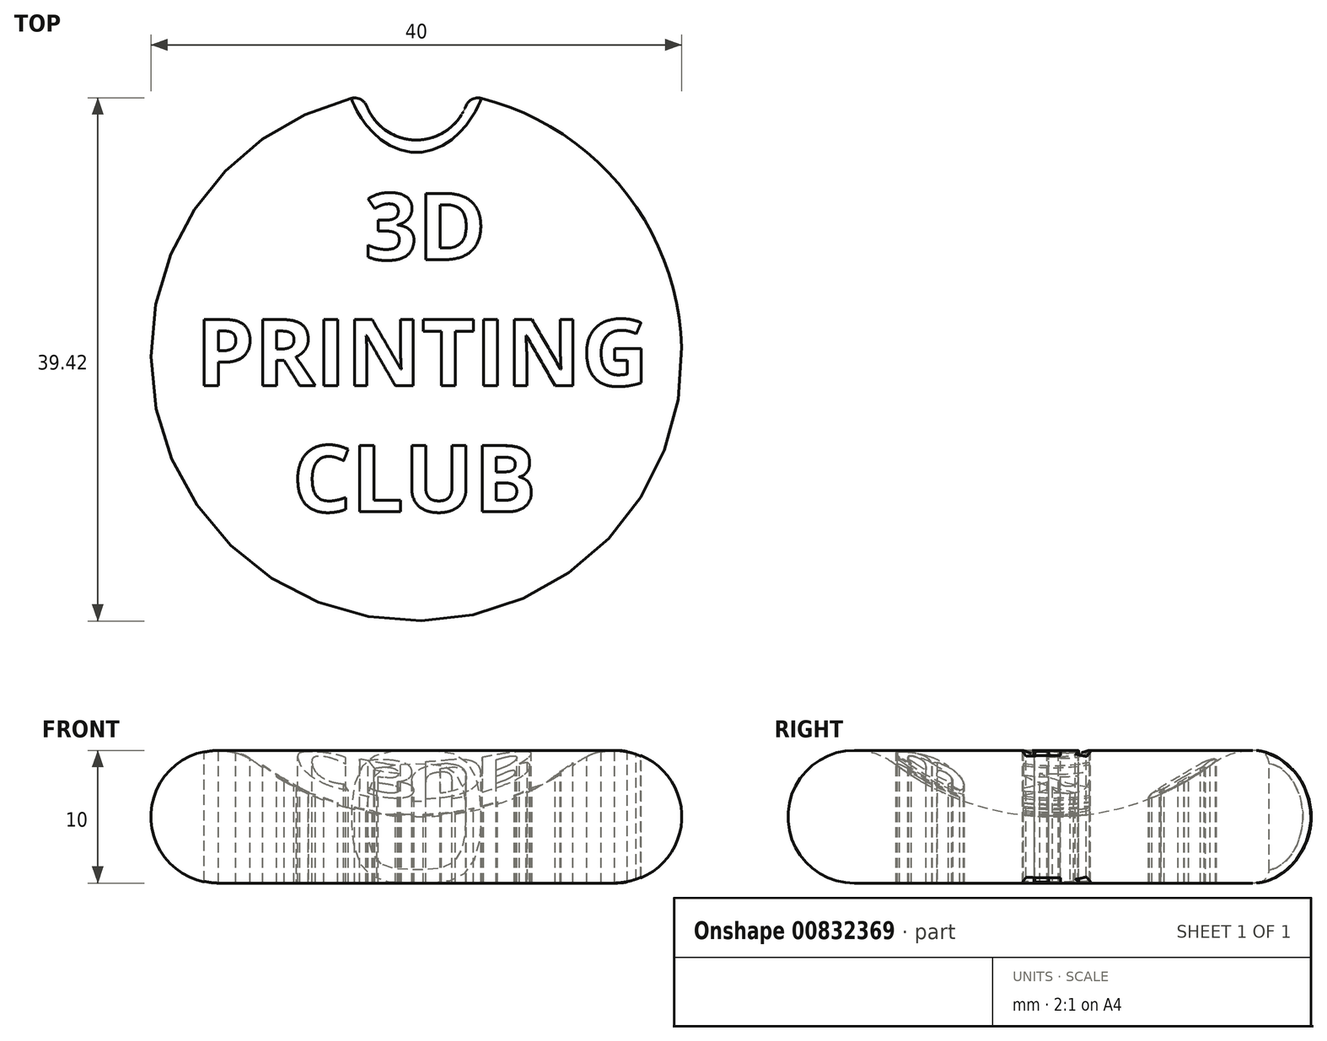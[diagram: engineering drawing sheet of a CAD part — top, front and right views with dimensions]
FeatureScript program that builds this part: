
annotation { "Feature Type Name" : "Feature", "Feature Type Description" : "" }
export const myFeature = defineFeature(function(context is Context, id is Id, definition is map)
    precondition{}
    {
        {
            var Q0;
            Q0=qCreatedBy(makeId("Front.planeOp"),FACE);
            var sketch = newSketch(context, id + "F0", { "sketchPlane" : qUnion([Q0])});
            skArc(sketch, "E0", {"start": v(-12, 9) * mm, "mid": v(-6.32, 6.03) * mm, "end": v(0, 5) * mm});
            skArc(sketch, "E1", {"start": v(-12, 9) * mm, "mid": v(-19.74, 6.58) * mm, "end": v(-15, 0) * mm});
            skLineSegment(sketch, "E2", {"start": v(0, 5) * mm, "end": v(0, 0) * mm});
            skLineSegment(sketch, "E3", {"start": v(0, 0) * mm, "end": v(-15, 0) * mm});
            skSolve(sketch);
        }
        {
            var Q0;
            Q0=makeQuery(id+"F0.imprint","IMPRINT",FACE,{"disambiguationData":[TD([[makeQuery(id+"F0.imprint","IMPRINT",EDGE,{"derivedFrom":sQuery(id+"F0.wireOp",EDGE,"E0")}),-1.0]])]});
            var Q1;
            Q1=sQuery(id+"F0.wireOp",EDGE,"E2");
            revolve(context, id + "F1", {"surfaceOperationType" : NewSurfaceOperationType.NEW, "entities" : qUnion([Q0]), "axis" : qUnion([Q1]), "revolveType" : RevolveType.FULL});
        }
        {
            var Q0;
            Q0=qCreatedBy(makeId("Top.planeOp"),FACE);
            cPlane(context, id + "F2", {"entities" : qUnion([Q0]), "cplaneType" : CPlaneType.OFFSET, "offset" : 10 * mm, "width" : 150 * mm, "height" : 150 * mm});
        }
        {
            var Q0;
            Q0=qCreatedBy(id+"F2.planeOp",FACE);
            var sketch = newSketch(context, id + "F3", { "sketchPlane" : qUnion([Q0])});
            skText(sketch, "E4", { "text": "       3D \nPRINTING\n    CLUB", "fontName": "OpenSans-Bold.ttf"});
            const initialGuessF3  = {"E4": [-0.0166, 0.00723, 1, 0, 0.00503]};
            skSetInitialGuess(sketch, initialGuessF3);
            skSolve(sketch);
        }
        {
            var Q0;
            Q0 = qSketchRegion(id + "F3", true);
            extrude(context, id + "F4", {"entities" : qUnion([Q0]), "operationType" : NewBodyOperationType.REMOVE, "oppositeDirection" : true, "depth" : 25 * mm, "offsetDistance" : 25 * mm});
        }
        {
            var Q0;
            Q0=qCreatedBy(id+"F2.planeOp",FACE);
            var sketch = newSketch(context, id + "F5", { "sketchPlane" : qUnion([Q0])});
            skCircle(sketch, "E5", {"center": v(0, 20.25) * mm, "radius": 4 * mm});
            skSolve(sketch);
        }
        {
            var Q0;
            Q0 = qSketchRegion(id + "F5", true);
            extrude(context, id + "F6", {"entities" : qUnion([Q0]), "operationType" : NewBodyOperationType.REMOVE, "oppositeDirection" : true, "depth" : 25 * mm, "offsetDistance" : 25 * mm});
        }
        {
            var Q0;
            Q0=makeQuery(id+"F6.boolean.opBoolean","INTERSECT",EDGE,{"derivedFrom":[makeQuery(id+"F4.boolean.opBoolean","SPLIT",FACE,{"disambiguationData":[TD([makeQuery(id+"F1.opRevolve","SWEPT_FACE",FACE,{"disambiguationData":[OSD([sQuery(id+"F0.wireOp",EDGE,"E0")])]}),makeQuery(id+"F1.opRevolve","SWEPT_FACE",FACE,{"disambiguationData":[OSD([sQuery(id+"F0.wireOp",EDGE,"E3")])]}),makeQuery(id+"F4.opExtrude","SWEPT_FACE",FACE,{"disambiguationData":[OSD([sQuery(id+"F3.wireOp",EDGE,"E4.sketch_text.stroke-20")])]}),makeQuery(id+"F4.opExtrude","SWEPT_FACE",FACE,{"disambiguationData":[OSD([sQuery(id+"F3.wireOp",EDGE,"E4.sketch_text.stroke-21")])]}),makeQuery(id+"F4.opExtrude","SWEPT_FACE",FACE,{"disambiguationData":[OSD([sQuery(id+"F3.wireOp",EDGE,"E4.sketch_text.stroke-22")])]}),makeQuery(id+"F4.opExtrude","SWEPT_FACE",FACE,{"disambiguationData":[OSD([sQuery(id+"F3.wireOp",EDGE,"E4.sketch_text.stroke-23")])]}),makeQuery(id+"F4.opExtrude","SWEPT_FACE",FACE,{"disambiguationData":[OSD([sQuery(id+"F3.wireOp",EDGE,"E4.sketch_text.stroke-24")])]}),makeQuery(id+"F4.opExtrude","SWEPT_FACE",FACE,{"disambiguationData":[OSD([sQuery(id+"F3.wireOp",EDGE,"E4.sketch_text.stroke-25")])]}),makeQuery(id+"F4.opExtrude","SWEPT_FACE",FACE,{"disambiguationData":[OSD([sQuery(id+"F3.wireOp",EDGE,"E4.sketch_text.stroke-26")])]}),makeQuery(id+"F4.opExtrude","SWEPT_FACE",FACE,{"disambiguationData":[OSD([sQuery(id+"F3.wireOp",EDGE,"E4.sketch_text.stroke-30")])]}),makeQuery(id+"F4.opExtrude","SWEPT_FACE",FACE,{"disambiguationData":[OSD([sQuery(id+"F3.wireOp",EDGE,"E4.sketch_text.stroke-31")])]}),makeQuery(id+"F4.opExtrude","SWEPT_FACE",FACE,{"disambiguationData":[OSD([sQuery(id+"F3.wireOp",EDGE,"E4.sketch_text.stroke-32")])]}),makeQuery(id+"F4.opExtrude","SWEPT_FACE",FACE,{"disambiguationData":[OSD([sQuery(id+"F3.wireOp",EDGE,"E4.sketch_text.stroke-46")])]}),makeQuery(id+"F4.opExtrude","SWEPT_FACE",FACE,{"disambiguationData":[OSD([sQuery(id+"F3.wireOp",EDGE,"E4.sketch_text.stroke-47")])]}),makeQuery(id+"F4.opExtrude","SWEPT_FACE",FACE,{"disambiguationData":[OSD([sQuery(id+"F3.wireOp",EDGE,"E4.sketch_text.stroke-48")])]}),makeQuery(id+"F4.opExtrude","SWEPT_FACE",FACE,{"disambiguationData":[OSD([sQuery(id+"F3.wireOp",EDGE,"E4.sketch_text.stroke-49")])]}),makeQuery(id+"F4.opExtrude","SWEPT_FACE",FACE,{"disambiguationData":[OSD([sQuery(id+"F3.wireOp",EDGE,"E4.sketch_text.stroke-50")])]}),makeQuery(id+"F4.opExtrude","SWEPT_FACE",FACE,{"disambiguationData":[OSD([sQuery(id+"F3.wireOp",EDGE,"E4.sketch_text.stroke-51")])]}),makeQuery(id+"F4.opExtrude","SWEPT_FACE",FACE,{"disambiguationData":[OSD([sQuery(id+"F3.wireOp",EDGE,"E4.sketch_text.stroke-52")])]}),makeQuery(id+"F4.opExtrude","SWEPT_FACE",FACE,{"disambiguationData":[OSD([sQuery(id+"F3.wireOp",EDGE,"E4.sketch_text.stroke-53")])]}),makeQuery(id+"F4.opExtrude","SWEPT_FACE",FACE,{"disambiguationData":[OSD([sQuery(id+"F3.wireOp",EDGE,"E4.sketch_text.stroke-54")])]}),makeQuery(id+"F4.opExtrude","SWEPT_FACE",FACE,{"disambiguationData":[OSD([sQuery(id+"F3.wireOp",EDGE,"E4.sketch_text.stroke-104")])]}),makeQuery(id+"F4.opExtrude","SWEPT_FACE",FACE,{"disambiguationData":[OSD([sQuery(id+"F3.wireOp",EDGE,"E4.sketch_text.stroke-116")])]}),makeQuery(id+"F4.opExtrude","SWEPT_FACE",FACE,{"disambiguationData":[OSD([sQuery(id+"F3.wireOp",EDGE,"E4.sketch_text.stroke-117")])]}),makeQuery(id+"F4.opExtrude","SWEPT_FACE",FACE,{"disambiguationData":[OSD([sQuery(id+"F3.wireOp",EDGE,"E4.sketch_text.stroke-118")])]}),makeQuery(id+"F4.opExtrude","SWEPT_FACE",FACE,{"disambiguationData":[OSD([sQuery(id+"F3.wireOp",EDGE,"E4.sketch_text.stroke-119")])]}),makeQuery(id+"F4.opExtrude","SWEPT_FACE",FACE,{"disambiguationData":[OSD([sQuery(id+"F3.wireOp",EDGE,"E4.sketch_text.stroke-120")])]}),makeQuery(id+"F4.opExtrude","SWEPT_FACE",FACE,{"disambiguationData":[OSD([sQuery(id+"F3.wireOp",EDGE,"E4.sketch_text.stroke-121")])]}),makeQuery(id+"F4.opExtrude","SWEPT_FACE",FACE,{"disambiguationData":[OSD([sQuery(id+"F3.wireOp",EDGE,"E4.sketch_text.stroke-122")])]}),makeQuery(id+"F4.opExtrude","SWEPT_FACE",FACE,{"disambiguationData":[OSD([sQuery(id+"F3.wireOp",EDGE,"E4.sketch_text.stroke-123")])]}),makeQuery(id+"F4.opExtrude","SWEPT_FACE",FACE,{"disambiguationData":[OSD([sQuery(id+"F3.wireOp",EDGE,"E4.sketch_text.stroke-124")])]}),makeQuery(id+"F4.opExtrude","SWEPT_FACE",FACE,{"disambiguationData":[OSD([sQuery(id+"F3.wireOp",EDGE,"E4.sketch_text.stroke-125")])]}),makeQuery(id+"F4.opExtrude","SWEPT_FACE",FACE,{"disambiguationData":[OSD([sQuery(id+"F3.wireOp",EDGE,"E4.sketch_text.stroke-126")])]}),makeQuery(id+"F4.opExtrude","SWEPT_FACE",FACE,{"disambiguationData":[OSD([sQuery(id+"F3.wireOp",EDGE,"E4.sketch_text.stroke-127")])]}),makeQuery(id+"F4.opExtrude","SWEPT_FACE",FACE,{"disambiguationData":[OSD([sQuery(id+"F3.wireOp",EDGE,"E4.sketch_text.stroke-128")])]}),makeQuery(id+"F4.opExtrude","SWEPT_FACE",FACE,{"disambiguationData":[OSD([sQuery(id+"F3.wireOp",EDGE,"E4.sketch_text.stroke-129")])]}),makeQuery(id+"F4.opExtrude","SWEPT_FACE",FACE,{"disambiguationData":[OSD([sQuery(id+"F3.wireOp",EDGE,"E4.sketch_text.stroke-130")])]}),makeQuery(id+"F4.opExtrude","SWEPT_FACE",FACE,{"disambiguationData":[OSD([sQuery(id+"F3.wireOp",EDGE,"E4.sketch_text.stroke-131")])]}),makeQuery(id+"F4.opExtrude","SWEPT_FACE",FACE,{"disambiguationData":[OSD([sQuery(id+"F3.wireOp",EDGE,"E4.sketch_text.stroke-132")])]}),makeQuery(id+"F4.opExtrude","SWEPT_FACE",FACE,{"disambiguationData":[OSD([sQuery(id+"F3.wireOp",EDGE,"E4.sketch_text.stroke-133")])]}),makeQuery(id+"F4.opExtrude","SWEPT_FACE",FACE,{"disambiguationData":[OSD([sQuery(id+"F3.wireOp",EDGE,"E4.sketch_text.stroke-134")])]}),makeQuery(id+"F4.opExtrude","SWEPT_FACE",FACE,{"disambiguationData":[OSD([sQuery(id+"F3.wireOp",EDGE,"E4.sketch_text.stroke-135")])]}),makeQuery(id+"F4.opExtrude","SWEPT_FACE",FACE,{"disambiguationData":[OSD([sQuery(id+"F3.wireOp",EDGE,"E4.sketch_text.stroke-136")])]}),makeQuery(id+"F4.opExtrude","SWEPT_FACE",FACE,{"disambiguationData":[OSD([sQuery(id+"F3.wireOp",EDGE,"E4.sketch_text.stroke-137")])]}),makeQuery(id+"F4.opExtrude","SWEPT_FACE",FACE,{"disambiguationData":[OSD([sQuery(id+"F3.wireOp",EDGE,"E4.sketch_text.stroke-138")])]}),makeQuery(id+"F4.opExtrude","SWEPT_FACE",FACE,{"disambiguationData":[OSD([sQuery(id+"F3.wireOp",EDGE,"E4.sketch_text.stroke-139")])]}),makeQuery(id+"F4.opExtrude","SWEPT_FACE",FACE,{"disambiguationData":[OSD([sQuery(id+"F3.wireOp",EDGE,"E4.sketch_text.stroke-140")])]}),makeQuery(id+"F4.opExtrude","SWEPT_FACE",FACE,{"disambiguationData":[OSD([sQuery(id+"F3.wireOp",EDGE,"E4.sketch_text.stroke-141")])]}),makeQuery(id+"F4.opExtrude","SWEPT_FACE",FACE,{"disambiguationData":[OSD([sQuery(id+"F3.wireOp",EDGE,"E4.sketch_text.stroke-142")])]}),makeQuery(id+"F4.opExtrude","SWEPT_FACE",FACE,{"disambiguationData":[OSD([sQuery(id+"F3.wireOp",EDGE,"E4.sketch_text.stroke-143")])]}),makeQuery(id+"F4.opExtrude","SWEPT_FACE",FACE,{"disambiguationData":[OSD([sQuery(id+"F3.wireOp",EDGE,"E4.sketch_text.stroke-144")])]}),makeQuery(id+"F4.opExtrude","SWEPT_FACE",FACE,{"disambiguationData":[OSD([sQuery(id+"F3.wireOp",EDGE,"E4.sketch_text.stroke-145")])]}),makeQuery(id+"F4.opExtrude","SWEPT_FACE",FACE,{"disambiguationData":[OSD([sQuery(id+"F3.wireOp",EDGE,"E4.sketch_text.stroke-146")])]}),makeQuery(id+"F4.opExtrude","SWEPT_FACE",FACE,{"disambiguationData":[OSD([sQuery(id+"F3.wireOp",EDGE,"E4.sketch_text.stroke-152")])]}),makeQuery(id+"F4.opExtrude","SWEPT_FACE",FACE,{"disambiguationData":[OSD([sQuery(id+"F3.wireOp",EDGE,"E4.sketch_text.stroke-156")])]}),makeQuery(id+"F4.opExtrude","SWEPT_FACE",FACE,{"disambiguationData":[OSD([sQuery(id+"F3.wireOp",EDGE,"E4.sketch_text.stroke-157")])]}),makeQuery(id+"F4.opExtrude","SWEPT_FACE",FACE,{"disambiguationData":[OSD([sQuery(id+"F3.wireOp",EDGE,"E4.sketch_text.stroke-180")])]}),makeQuery(id+"F4.opExtrude","SWEPT_FACE",FACE,{"disambiguationData":[OSD([sQuery(id+"F3.wireOp",EDGE,"E4.sketch_text.stroke-181")])]}),makeQuery(id+"F4.opExtrude","SWEPT_FACE",FACE,{"disambiguationData":[OSD([sQuery(id+"F3.wireOp",EDGE,"E4.sketch_text.stroke-182")])]}),makeQuery(id+"F4.opExtrude","SWEPT_FACE",FACE,{"disambiguationData":[OSD([sQuery(id+"F3.wireOp",EDGE,"E4.sketch_text.stroke-183")])]}),makeQuery(id+"F4.opExtrude","SWEPT_FACE",FACE,{"disambiguationData":[OSD([sQuery(id+"F3.wireOp",EDGE,"E4.sketch_text.stroke-184")])]})])],"derivedFrom":makeQuery(id+"F1.opRevolve","SWEPT_FACE",FACE,{"disambiguationData":[OSD([sQuery(id+"F0.wireOp",EDGE,"E1")])]})}),makeQuery(id+"F6.opExtrude","SWEPT_FACE",FACE,{"disambiguationData":[OSD([sQuery(id+"F5.wireOp",EDGE,"E5")])]})]});
            fillet(context, id + "F7", {"entities" : qUnion([Q0]), "radius" : 1 * mm, "tangentPropagation" : true, "allowEdgeOverflow" : false});
        }
    });
